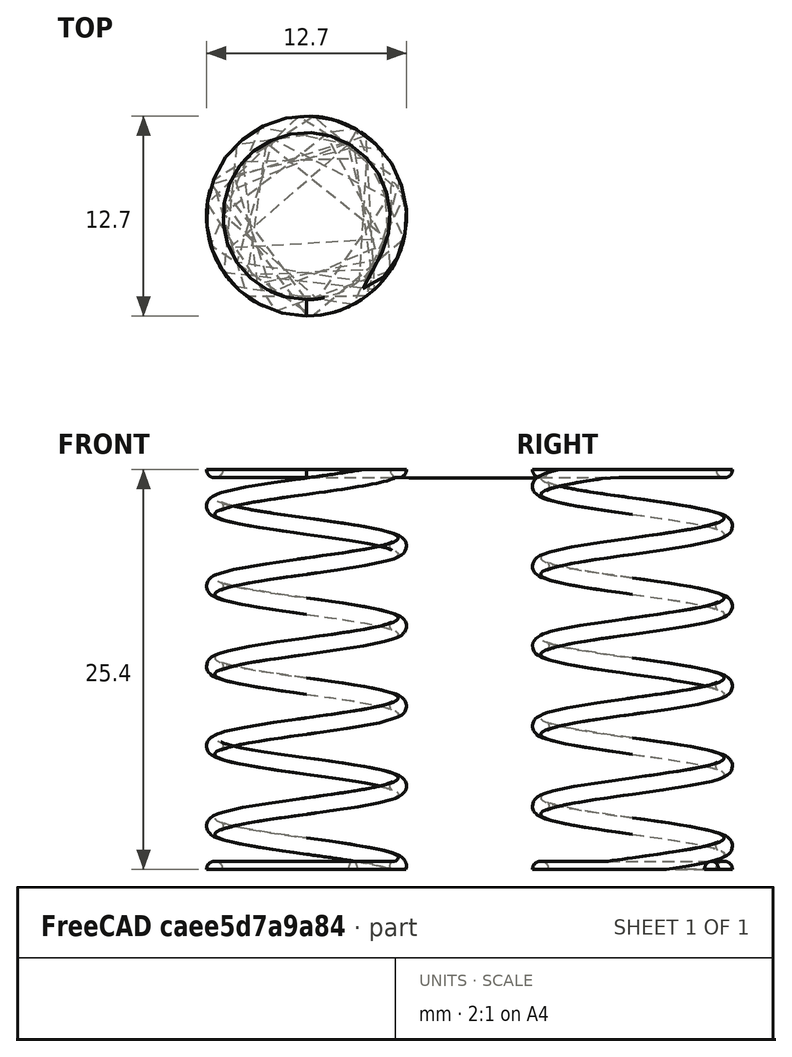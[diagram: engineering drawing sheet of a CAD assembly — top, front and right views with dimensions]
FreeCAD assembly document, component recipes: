
FREECAD ASSEMBLY — COMPONENT RECIPES ("mag-clamp")

This assembly document has 10 components, labeled P0..P9 below (a component is one placed body or linked part). 4 of them carry a construction recipe — the FreeCAD feature program that regenerates the part from scratch, quoted from this document or its linked companion documents; the rest are supplied as boundary geometry only. No exploded tour is included for this assembly.
COMPONENT P0 — recipe-attached ("Base001", modeled in this document).
Construction recipe (the document's own serialized feature program — sketch geometry with constraints, then the solid features built on it; lengths are millimeters unless a unit is written):

FEATURE [Sketcher::SketchObject] Sketch
  ArcFitTolerance = 1e-06
  AttachmentSupport = -> [XZ_Plane]
  FullyConstrained = true
  MakeInternals = false
  MapMode = 5
  Placement = pos=(0,0,0) rot=(1,0,0;1.5708rad)
  expr: Constraints[22] = VarSet.height
  sketch-geometry (14):
    g0: LineSegment StartX=0 StartY=0 StartZ=0 EndX=12 EndY=0 EndZ=0
    g1: LineSegment StartX=7 StartY=20.325 StartZ=0 EndX=7 EndY=18.325 EndZ=0
    g2: LineSegment StartX=9 StartY=30.325 StartZ=0 EndX=11 EndY=30.325 EndZ=0
    g3: LineSegment [constr] StartX=7 StartY=18.325 StartZ=0 EndX=5 EndY=18.325 EndZ=0
    g4: LineSegment [constr] StartX=5 StartY=18.325 StartZ=0 EndX=5 EndY=20.325 EndZ=0
    g5: LineSegment [constr] StartX=5 StartY=20.325 StartZ=0 EndX=0 EndY=20.325 EndZ=0
    g6: LineSegment StartX=0 StartY=0 StartZ=0 EndX=0 EndY=20.325 EndZ=0
    g7: LineSegment StartX=7 StartY=20.325 StartZ=0 EndX=9 EndY=20.325 EndZ=0
    g8: LineSegment StartX=9 StartY=20.325 StartZ=0 EndX=9 EndY=30.325 EndZ=0
    g9: LineSegment [constr] StartX=5 StartY=20.325 StartZ=0 EndX=7 EndY=20.325 EndZ=0
    g10: LineSegment StartX=11 StartY=30.325 StartZ=0 EndX=11 EndY=8 EndZ=0
    g11: LineSegment StartX=12 StartY=0 StartZ=0 EndX=12 EndY=1 EndZ=0
    g12: ArcOfCircle CenterX=15 CenterY=5 CenterZ=0 NormalX=0 NormalY=0 NormalZ=1 AngleXU=0 Radius=5 StartAngle=2.49809 EndAngle=4.06889
    g13: LineSegment StartX=0 StartY=20.325 StartZ=0 EndX=7 EndY=18.325 EndZ=0
  constraints (40):
    c: Coincident(g-1,g0)
    c: PointOnObject(g0,g-1)
    c: Vertical(g1)
    c: Horizontal(g3)
    c: Vertical(g4)
    c: Coincident(g5,g4)
    c: Horizontal(g5)
    c: Coincident(g3,g1)
    c: Horizontal(g2)
    c: Coincident(g3,g4)
    c: DistanceX(g6,g3) = 5
    c: Coincident(g6,g0)
    c: DistanceX(g0,g1) = 7
    c: DistanceX(g0,g0) = 12
    c: DistanceY(g4,g4) = 2
    c: Coincident(g6,g5)
    c: PointOnObject(g5,g-2)
    c: Horizontal(g7)
    c: Coincident(g7,g8)
    c: Vertical(g8)
    c: Coincident(g1,g7)
    c: Coincident(g2,g8)
    c: DistanceY(g0,g2) = 30.325
    c: DistanceY(g8,g8) = 10
    c: DistanceX(g7,g7) = 2
    c: DistanceX(g2,g2) = 2
    c: Coincident(g9,g4)
    c: Coincident(g9,g1)
    c: Horizontal(g9)
    c: Coincident(g10,g2)
    c: Vertical(g10)
    c: Coincident(g11,g0)
    c: Coincident(g12,g11)
    c: Coincident(g12,g10)
    c: Vertical(g11)
    c: DistanceY(g11,g11) = 1
    c: Radius(g12) = 5
    c: DistanceY(g0,g10) = 8
    c: Coincident(g13,g5)
    c: Coincident(g13,g1)
FEATURE [PartDesign::Revolution] Revolution
  Angle = 360
  Angle2 = 60
  Axis = (0,2e-16,1)
  Base = (0,0,0)
  Placement = pos=(0,0,0) rot=(1,0,0;1.5708rad)
  Profile = -> Sketch
  ReferenceAxis = -> Sketch [V_Axis]
  Refine = true
  Reversed = true
  Suppressed = false
  Type = 0
FEATURE [PartDesign::Fillet] Fillet001
  Base = -> Revolution [Edge6,Edge12,Edge9]
  BaseFeature = -> Revolution
  Placement = pos=(0,0,0) rot=(1,0,0;1.5708rad)
  Radius = 1
  Refine = true
  SupportTransform = false
  Suppressed = false
  UseAllEdges = false
FEATURE [Sketcher::SketchObject] Sketch010
  ArcFitTolerance = 1e-06
  AttachmentSupport = -> [Fillet001]
  FullyConstrained = true
  MakeInternals = false
  MapMode = 5
  Placement = pos=(0,6.7e-15,30.325) rot=(0,0,1;3.14159rad)
  expr: Constraints[1] = VarSet.heatset_od
  sketch-geometry (1):
    g0: Circle CenterX=0 CenterY=0 CenterZ=0 NormalX=0 NormalY=0 NormalZ=1 AngleXU=0 Radius=2.75
  constraints (2):
    c: Coincident(g0,g-1)
    c: Diameter(g0) = 5.5
FEATURE [PartDesign::Pocket] Pocket
  BaseFeature = -> Fillet001
  Direction = (0,0,-1)
  Length = 5
  Length2 = 5
  Placement = pos=(0,0,0) rot=(1,0,0;1.5708rad)
  Profile = -> Sketch010
  ReferenceAxis = -> Sketch010 [N_Axis]
  Refine = true
  Suppressed = false
  Type = 1
FEATURE [PartDesign::Fillet] Fillet002
  Base = -> Pocket [Edge3]
  BaseFeature = -> Pocket
  Placement = pos=(0,0,0) rot=(1,0,0;1.5708rad)
  Radius = 2
  Refine = true
  SupportTransform = false
  Suppressed = false
  UseAllEdges = false
FEATURE [PartDesign::Body] Body  label="Base"
  AllowCompound = false
  Group = -> [Sketch,Revolution,Fillet001,Sketch010,Pocket,Fillet002]
  Origin = -> Origin
  Tip = -> Fillet002
COMPONENT P1 — recipe-attached ("Cap001", modeled in this document).
Construction recipe (the document's own serialized feature program — sketch geometry with constraints, then the solid features built on it; lengths are millimeters unless a unit is written):

FEATURE [Sketcher::SketchObject] Sketch003
  ArcFitTolerance = 1e-06
  AttachmentSupport = -> [XZ_Plane002]
  FullyConstrained = false
  MakeInternals = false
  MapMode = 5
  Placement = pos=(0,0,0) rot=(1,0,0;1.5708rad)
  sketch-geometry (4):
    g0: LineSegment StartX=0 StartY=36.6662 StartZ=0 EndX=0 EndY=33.6662 EndZ=0
    g1: LineSegment StartX=0 StartY=33.6662 StartZ=0 EndX=8.5 EndY=33.6662 EndZ=0
    g2: LineSegment StartX=8.5 StartY=33.6662 StartZ=0 EndX=8.5 EndY=36.6662 EndZ=0
    g3: LineSegment StartX=8.5 StartY=36.6662 StartZ=0 EndX=0 EndY=36.6662 EndZ=0
  constraints (11):
    c: Coincident(g0,g1)
    c: Coincident(g1,g2)
    c: Coincident(g2,g3)
    c: Coincident(g3,g0)
    c: Vertical(g0)
    c: Vertical(g2)
    c: Horizontal(g1)
    c: Horizontal(g3)
    c: PointOnObject(g0,g-2)
    c: DistanceX(g3,g3) = 8.5
    c: Distance(g2,g2) = 3
FEATURE [PartDesign::Revolution] Revolution002
  Angle = 360
  Angle2 = 60
  Axis = (0,2e-16,1)
  Base = (0,0,0)
  Placement = pos=(0,0,0) rot=(1,0,0;1.5708rad)
  Profile = -> Sketch003
  ReferenceAxis = -> Sketch003 [V_Axis]
  Refine = true
  Reversed = true
  Suppressed = false
  Type = 0
FEATURE [PartDesign::Fillet] Fillet
  Base = -> Revolution002 [Edge2]
  BaseFeature = -> Revolution002
  Placement = pos=(0,0,0) rot=(1,0,0;1.5708rad)
  Radius = 1
  Refine = true
  SupportTransform = false
  Suppressed = false
  UseAllEdges = false
FEATURE [Sketcher::SketchObject] Sketch004
  ArcFitTolerance = 1e-06
  AttachmentSupport = -> [XZ_Plane002]
  ExternalGeometry = -> [Fillet]
  FullyConstrained = false
  MakeInternals = false
  MapMode = 5
  Placement = pos=(0,0,0) rot=(1,0,0;1.5708rad)
  sketch-geometry (5):
    g0: LineSegment StartX=0 StartY=36.6662 StartZ=0 EndX=0 EndY=29.3467 EndZ=0
    g1: LineSegment StartX=0 StartY=29.3467 StartZ=0 EndX=1.5 EndY=29.3467 EndZ=0
    g2: LineSegment StartX=0 StartY=36.6662 StartZ=0 EndX=3.2 EndY=36.6662 EndZ=0
    g3: LineSegment StartX=3.2 StartY=36.6662 StartZ=0 EndX=1.5 EndY=34.9662 EndZ=0
    g4: LineSegment StartX=1.5 StartY=34.9662 StartZ=0 EndX=1.5 EndY=29.3467 EndZ=0
  constraints (14):
    c: PointOnObject(g0,g-2)
    c: Vertical(g0)
    c: Coincident(g1,g0)
    c: Horizontal(g1)
    c: Coincident(g2,g0)
    c: Horizontal(g2)
    c: Coincident(g3,g2)
    c: Coincident(g4,g3)
    c: Coincident(g4,g1)
    c: Vertical(g4)
    c: DistanceX(g1,g1) = 1.5
    c: Angle(g3,g-2) = 0.785398
    c: PointOnObject(g2,g-3)
    c: DistanceY(g3,g-3) = 1.7
FEATURE [PartDesign::Groove] Groove
  Angle = 360
  Angle2 = 60
  Axis = (0,2e-16,1)
  Base = (0,0,0)
  BaseFeature = -> Fillet
  Placement = pos=(0,0,0) rot=(1,0,0;1.5708rad)
  Profile = -> Sketch004
  ReferenceAxis = -> Sketch004 [V_Axis]
  Refine = true
  Suppressed = false
  Type = 0
FEATURE [PartDesign::Body] Body002  label="Cap"
  AllowCompound = false
  Group = -> [Sketch003,Revolution002,Fillet,Sketch004,Groove]
  Origin = -> Origin002
  Tip = -> Groove
COMPONENT P2 — recipe-attached ("Magnet001", modeled in this document).
Construction recipe (the document's own serialized feature program — sketch geometry with constraints, then the solid features built on it; lengths are millimeters unless a unit is written):

FEATURE [Sketcher::SketchObject] Sketch005
  ArcFitTolerance = 1e-06
  AttachmentSupport = -> [XZ_Plane003]
  FullyConstrained = true
  MakeInternals = false
  MapMode = 5
  Placement = pos=(0,0,0) rot=(1,0,0;1.5708rad)
  expr: Constraints[14] = VarSet.bottom_thk
  expr: Constraints[15] = VarSet.magnet_od / 2 + 0.25 mm
  sketch-geometry (6):
    g0: LineSegment StartX=0 StartY=0 StartZ=0 EndX=12 EndY=0 EndZ=0
    g1: LineSegment StartX=12 StartY=0 StartZ=0 EndX=12 EndY=-4.175 EndZ=0
    g2: LineSegment StartX=12 StartY=-4.175 StartZ=0 EndX=5.0125 EndY=-4.175 EndZ=0
    g3: LineSegment StartX=5.0125 StartY=-4.175 StartZ=0 EndX=5.0125 EndY=-0.5 EndZ=0
    g4: LineSegment StartX=5.0125 StartY=-0.5 StartZ=0 EndX=0 EndY=-0.5 EndZ=0
    g5: LineSegment StartX=0 StartY=-0.5 StartZ=0 EndX=0 EndY=0 EndZ=0
  constraints (17):
    c: Coincident(g-1,g0)
    c: PointOnObject(g0,g-1)
    c: Coincident(g0,g1)
    c: Vertical(g1)
    c: Coincident(g1,g2)
    c: Horizontal(g2)
    c: Coincident(g2,g3)
    c: Vertical(g3)
    c: Coincident(g3,g4)
    c: PointOnObject(g4,g-2)
    c: Horizontal(g4)
    c: Coincident(g4,g5)
    c: Coincident(g5,g0)
    c: DistanceX(g0,g0) = 12
    c: DistanceY(g1,g1) = 4.175
    c: DistanceX(g4,g4) = 5.0125
    c: DistanceY(g5,g5) = 0.5
FEATURE [PartDesign::Revolution] Revolution003
  Angle = 360
  Angle2 = 60
  Axis = (0,2e-16,1)
  Base = (0,0,0)
  Placement = pos=(0,0,0) rot=(1,0,0;1.5708rad)
  Profile = -> Sketch005
  ReferenceAxis = -> Sketch005 [V_Axis]
  Refine = true
  Reversed = true
  Suppressed = false
  Type = 0
FEATURE [Sketcher::SketchObject] Sketch006
  ArcFitTolerance = 1e-06
  AttachmentSupport = -> [Revolution003]
  FullyConstrained = true
  MakeInternals = false
  MapMode = 5
  Placement = pos=(0,-1e-16,-0.5) rot=(1,0,0;3.14159rad)
  sketch-geometry (1):
    g0: Circle CenterX=0 CenterY=0 CenterZ=0 NormalX=0 NormalY=0 NormalZ=1 AngleXU=0 Radius=1.75
  constraints (2):
    c: Coincident(g0,g-1)
    c: Diameter(g0) = 3.5
FEATURE [PartDesign::Pocket] Pocket001
  BaseFeature = -> Revolution003
  Direction = (0,0,1)
  Length = 5
  Length2 = 5
  Placement = pos=(0,0,0) rot=(1,0,0;1.5708rad)
  Profile = -> Sketch006
  ReferenceAxis = -> Sketch006 [N_Axis]
  Refine = true
  Suppressed = false
  Type = 1
FEATURE [PartDesign::Body] Body003  label="Magnet"
  AllowCompound = false
  Group = -> [Sketch005,Revolution003,Sketch006,Pocket001]
  Origin = -> Origin003
  Tip = -> Pocket001
COMPONENT P3 — recipe-attached ("Retainer001", modeled in this document).
Construction recipe (the document's own serialized feature program — sketch geometry with constraints, then the solid features built on it; lengths are millimeters unless a unit is written):

FEATURE [Sketcher::SketchObject] Sketch002
  ArcFitTolerance = 1e-06
  AttachmentSupport = -> [XZ_Plane001]
  FullyConstrained = true
  MakeInternals = false
  MapMode = 5
  Placement = pos=(0,0,0) rot=(1,0,0;1.5708rad)
  expr: Constraints[14] = VarSet.retainer_height
  sketch-geometry (6):
    g0: LineSegment StartX=1.75 StartY=33.5 StartZ=0 EndX=8.5 EndY=33.5 EndZ=0
    g1: LineSegment StartX=8.5 StartY=33.5 StartZ=0 EndX=8.5 EndY=15.5 EndZ=0
    g2: LineSegment StartX=8.5 StartY=15.5 StartZ=0 EndX=7 EndY=15.5 EndZ=0
    g3: LineSegment StartX=7 StartY=15.5 StartZ=0 EndX=7 EndY=32 EndZ=0
    g4: LineSegment StartX=7 StartY=32 StartZ=0 EndX=1.75 EndY=32 EndZ=0
    g5: LineSegment StartX=1.75 StartY=32 StartZ=0 EndX=1.75 EndY=33.5 EndZ=0
  constraints (18):
    c: Horizontal(g0)
    c: Coincident(g0,g1)
    c: Vertical(g1)
    c: Coincident(g1,g2)
    c: Horizontal(g2)
    c: Coincident(g2,g3)
    c: Vertical(g3)
    c: Coincident(g3,g4)
    c: Horizontal(g4)
    c: Coincident(g4,g5)
    c: Vertical(g5)
    c: Coincident(g0,g5)
    c: DistanceX(g2,g2) = 1.5
    c: DistanceY(g5,g5) = 1.5
    c: DistanceY(g1,g1) = 18
    c: DistanceX(g-1,g0) = 1.75
    c: DistanceX(g-1,g3) = 7
    c: DistanceY(g-1,g4) = 32
FEATURE [PartDesign::Revolution] Revolution001
  Angle = 360
  Angle2 = 60
  Axis = (0,2e-16,1)
  Base = (0,0,0)
  Placement = pos=(0,0,0) rot=(1,0,0;1.5708rad)
  Profile = -> Sketch002
  ReferenceAxis = -> Sketch002 [V_Axis]
  Refine = true
  Reversed = true
  Suppressed = false
  Type = 0
FEATURE [PartDesign::Fillet] Fillet003
  Base = -> Revolution001 [Edge3]
  BaseFeature = -> Revolution001
  Placement = pos=(0,0,0) rot=(1,0,0;1.5708rad)
  Radius = 1
  Refine = true
  SupportTransform = false
  Suppressed = false
  UseAllEdges = false
FEATURE [PartDesign::Fillet] Fillet004
  Base = -> Fillet003 [Edge10]
  BaseFeature = -> Fillet003
  Placement = pos=(0,0,0) rot=(1,0,0;1.5708rad)
  Radius = 1
  Refine = true
  SupportTransform = false
  Suppressed = false
  UseAllEdges = false
FEATURE [PartDesign::Body] Body001  label="Retainer"
  AllowCompound = false
  Group = -> [Sketch002,Revolution001,Fillet003,Fillet004]
  Origin = -> Origin001
  Tip = -> Fillet004
COMPONENT P4 — geometry summary ("Spring001"; no construction recipe available for this part):
  bounding box: 25.4 x 12.7 x 12.7 mm
  tessellated surface: 141,082 triangles
  volume: 180 mm^3 (4% of its bounding box)
COMPONENT P5 — geometry summary ("92125A128_18-8 Stainless Steel Hex Drive Flat Head Screw001"; no construction recipe available for this part):
  bounding box: 8.0 x 6.0 x 6.0 mm
  tessellated surface: 17,346 triangles
  volume: 59 mm^3 (21% of its bounding box)
  symmetry: revolution-symmetric about the z axis through its bounding-box center
COMPONENT P6 — geometry summary ("92125A140_18-8 Stainless Steel Hex Drive Flat Head Screw001"; no construction recipe available for this part):
  bounding box: 30.0 x 6.0 x 6.0 mm
  tessellated surface: 81,198 triangles
  volume: 183 mm^3 (17% of its bounding box)
  symmetry: revolution-symmetric about the z axis through its bounding-box center; mirror-symmetric across its x mid-plane, y mid-plane
COMPONENT P7 — geometry summary ("94180A331_Tapered Heat-Set Inserts for Plastic002"; no construction recipe available for this part):
  bounding box: 5.6 x 5.6 x 3.8 mm
  tessellated surface: 13,346 triangles
  volume: 56 mm^3 (48% of its bounding box)
  symmetry: 6-fold rotationally symmetric about the z axis
COMPONENT P8 — geometry summary ("94180A331_Tapered Heat-Set Inserts for Plastic003"; no construction recipe available for this part):
  bounding box: 5.6 x 5.6 x 3.8 mm
  tessellated surface: 13,346 triangles
  volume: 56 mm^3 (48% of its bounding box)
  symmetry: 6-fold rotationally symmetric about the z axis
COMPONENT P9 — geometry summary ("5862K919_Neodymium Magnet001"; no construction recipe available for this part):
  bounding box: 9.5 x 9.5 x 3.2 mm
  tessellated surface: 2,140 triangles
  volume: 191 mm^3 (66% of its bounding box)
  symmetry: 4-fold rotationally symmetric about the z axis; mirror-symmetric across its x mid-plane, y mid-plane
PROVENANCE & LICENSES
A FreeCAD (.FCStd) document from a public repository crawl; recipes are the document's own serialized feature recipes (and, for linked parts, companion documents' recipes).
License: as declared in the source repository (recorded in the dataset sidecar).
